# Revit family: 52037-presto
name_source: partatom
category: Plumbing Fixtures
units: mm (PartAtom-declared; Revit-internal decimal feet)

## family parameters
Always vertical = Yes
Cut with Voids When Loaded = No
Maintain Annotation Orientation = No
OmniClass Number = 23.45.00.00
OmniClass Title = Sanitary, Laundry, and Cleaning Equipment
Part Type = Normal
Room Calculation Point = No
Round Connector Dimension = Use Diameter
Shared = No
Work Plane-Based = Yes

## types (1)
- 52037-presto
    - Hydraulic supply = 12.5 "
    -Delivered with = 1 Brass clamping nut, 1 Gasket and 1 Washer / - 1 wall fixing rose / - 2 PEX Hoses with G1/2'' revolving nuts / - 2 check valves / - 2 stop valves and 2 Filter gaskets / - 1 Self-adhesive sticker and 1 Instruction manual
    > Installation = Recommended installation : 30 cm minimum between the sensor and the basin
    > Standards & approvals = ACS / - CE
    > Thermal resistance : = 75.0000 (h·ft²·°F)/BTU
    Default Elevation = 1219 mm
    Description = PRESTORIZON Cross-wall mixer sensor tap
    Manufacturer = presto
    Model = 52037
    RANGE = PRESTORIZON - Range of Wall-Mounted Sensor Taps
    Recommended pressure = 3.00 bar
    URL = https://www.prestodatashare.com
    brand = LES ROBINETS PRESTO
    flow = 3 L/min
    min pressure = 1.00 bar
    power = 0 VA
    pressure = 5.00 bar

## geometry (parser evidence)
native form markers: Sweep x3
no freeform markers — native parametric forms only
